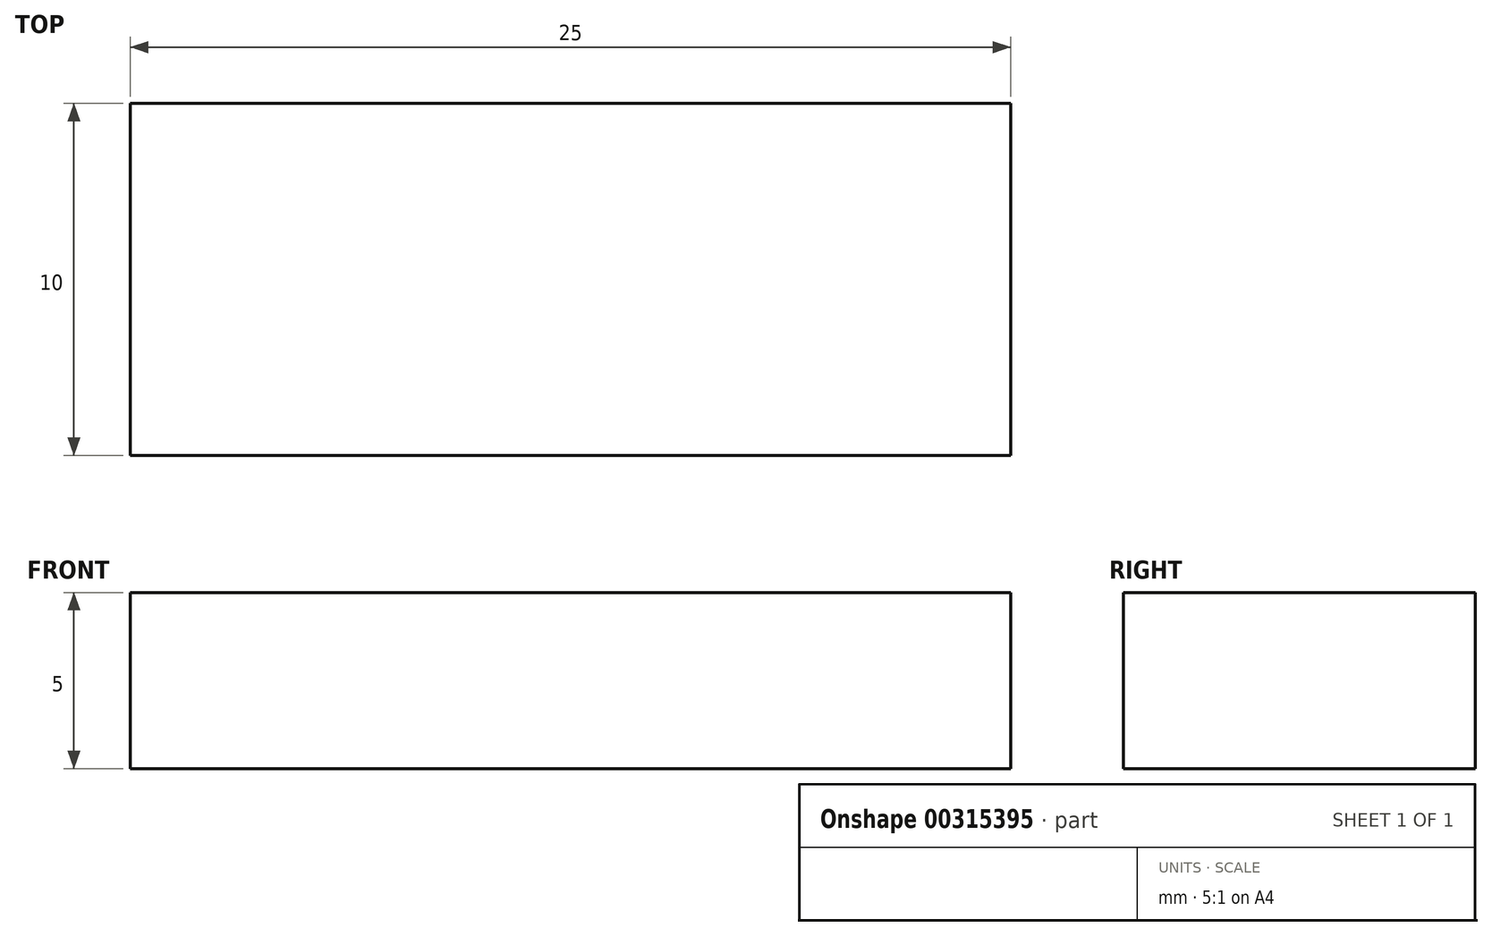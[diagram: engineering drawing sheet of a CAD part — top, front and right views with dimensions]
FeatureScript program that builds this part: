
annotation { "Feature Type Name" : "Feature", "Feature Type Description" : "" }
export const myFeature = defineFeature(function(context is Context, id is Id, definition is map)
    precondition{}
    {
        {
            var Q0;
            Q0=qCreatedBy(makeId("Front.planeOp"),FACE);
            var sketch = newSketch(context, id + "F0", { "sketchPlane" : qUnion([Q0])});
            skLineSegment(sketch, "E0.bottom", {"start": v(-12.5, 2.5) * mm, "end": v(12.5, 2.5) * mm});
            skLineSegment(sketch, "E0.top", {"start": v(-12.5, -2.5) * mm, "end": v(12.5, -2.5) * mm});
            skLineSegment(sketch, "E0.left", {"start": v(-12.5, 2.5) * mm, "end": v(-12.5, -2.5) * mm});
            skLineSegment(sketch, "E0.right", {"start": v(12.5, 2.5) * mm, "end": v(12.5, -2.5) * mm});
            skPoint(sketch, "E0.middle", {"position": v(0, 0) * mm});
            skSolve(sketch);
        }
        {
            var Q0;
            Q0=makeQuery(id+"F0.imprint","IMPRINT",FACE,{"disambiguationData":[TD([[makeQuery(id+"F0.imprint","IMPRINT",EDGE,{"derivedFrom":sQuery(id+"F0.wireOp",EDGE,"E0.bottom")}),-1.0]])]});
            extrude(context, id + "F1", {"entities" : qUnion([Q0]), "depth" : 10 * mm});
        }
    });
